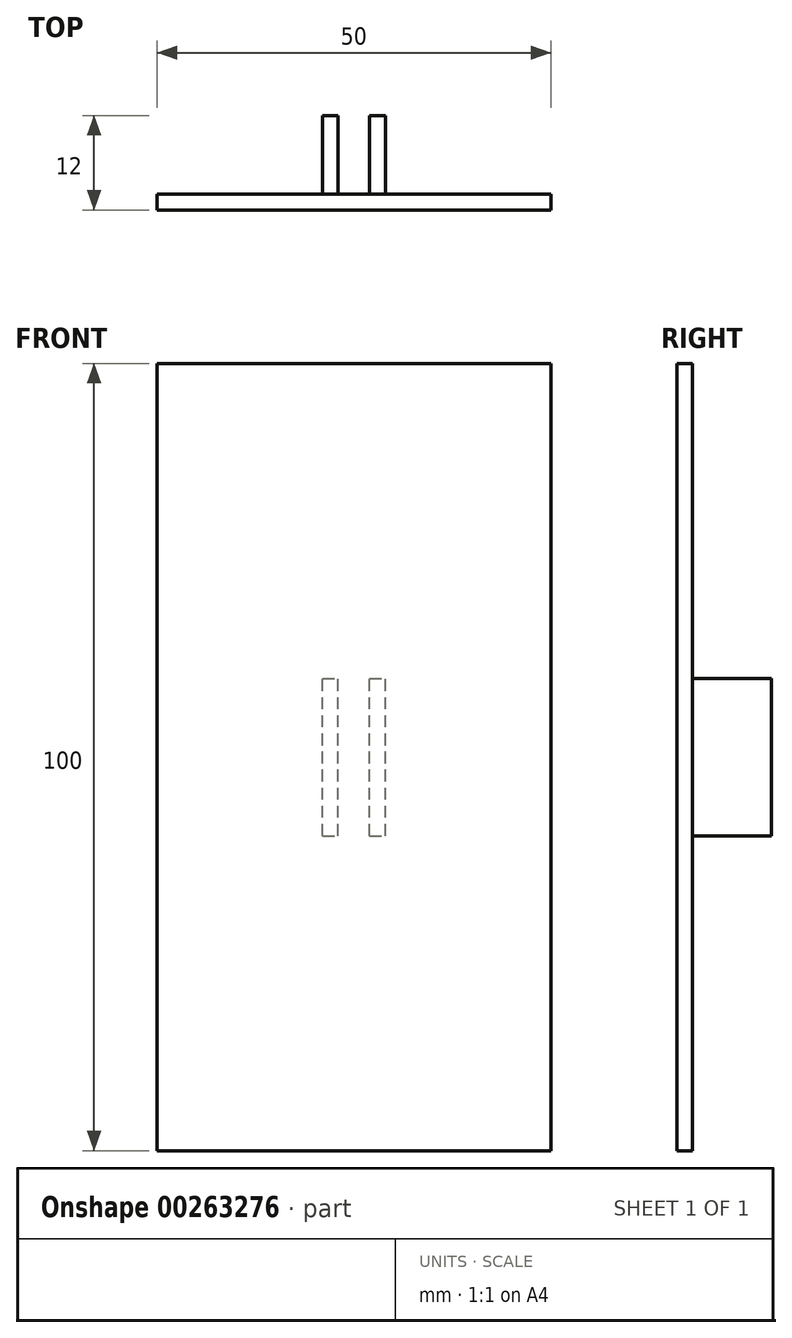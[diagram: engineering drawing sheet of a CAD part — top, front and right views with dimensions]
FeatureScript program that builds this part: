
annotation { "Feature Type Name" : "Feature", "Feature Type Description" : "" }
export const myFeature = defineFeature(function(context is Context, id is Id, definition is map)
    precondition{}
    {
        {
            var Q0;
            Q0=qCreatedBy(makeId("Front.planeOp"),FACE);
            var sketch = newSketch(context, id + "F0", { "sketchPlane" : qUnion([Q0])});
            skLineSegment(sketch, "E0.bottom", {"start": v(25, -50) * mm, "end": v(-25, -50) * mm});
            skLineSegment(sketch, "E0.top", {"start": v(25, 50) * mm, "end": v(-25, 50) * mm});
            skLineSegment(sketch, "E0.left", {"start": v(25, -50) * mm, "end": v(25, 50) * mm});
            skLineSegment(sketch, "E0.right", {"start": v(-25, -50) * mm, "end": v(-25, 50) * mm});
            skPoint(sketch, "E0.middle", {"position": v(0, 0) * mm});
            skSolve(sketch);
        }
        {
            var Q0;
            Q0=qSketchRegion(id+"F0",true);
            extrude(context, id + "F1", {"entities" : qUnion([Q0]), "depth" : 2 * mm});
        }
        {
            var Q0;
            Q0=makeQuery(id+"F1.opExtrude","CAP_FACE",FACE,{"disambiguationData":[OSD([sQuery(id+"F0.wireOp",EDGE,"E0.bottom"),sQuery(id+"F0.wireOp",EDGE,"E0.top"),sQuery(id+"F0.wireOp",EDGE,"E0.left"),sQuery(id+"F0.wireOp",EDGE,"E0.right")])],"isStart":true});
            var sketch = newSketch(context, id + "F2", { "sketchPlane" : qUnion([Q0])});
            skLineSegment(sketch, "E1.bottom", {"start": v(4, -10) * mm, "end": v(-4, -10) * mm});
            skLineSegment(sketch, "E1.top", {"start": v(4, 10) * mm, "end": v(-4, 10) * mm});
            skLineSegment(sketch, "E1.left", {"start": v(4, -10) * mm, "end": v(4, 10) * mm});
            skLineSegment(sketch, "E1.right", {"start": v(-4, -10) * mm, "end": v(-4, 10) * mm});
            skPoint(sketch, "E1.middle", {"position": v(0, 0) * mm});
            skSolve(sketch);
        }
        {
            var Q0;
            Q0 = qSketchRegion(id + "F2", true);
            extrude(context, id + "F3", {"entities" : qUnion([Q0]), "operationType" : NewBodyOperationType.ADD, "depth" : 10 * mm, "offsetDistance" : 25 * mm});
        }
        {
            var Q0;
            Q0=makeQuery(id+"F3.opExtrude","CAP_FACE",FACE,{"disambiguationData":[OSD([sQuery(id+"F2.wireOp",EDGE,"E1.bottom"),sQuery(id+"F2.wireOp",EDGE,"E1.top"),sQuery(id+"F2.wireOp",EDGE,"E1.left"),sQuery(id+"F2.wireOp",EDGE,"E1.right")])],"isStart":false});
            var sketch = newSketch(context, id + "F4", { "sketchPlane" : qUnion([Q0])});
            skLineSegment(sketch, "E2.bottom", {"start": v(2, -18.11) * mm, "end": v(-2, -18.11) * mm});
            skLineSegment(sketch, "E2.top", {"start": v(2, 18.11) * mm, "end": v(-2, 18.11) * mm});
            skLineSegment(sketch, "E2.left", {"start": v(2, -18.11) * mm, "end": v(2, 18.11) * mm});
            skLineSegment(sketch, "E2.right", {"start": v(-2, -18.11) * mm, "end": v(-2, 18.11) * mm});
            skPoint(sketch, "E2.middle", {"position": v(0, 0) * mm});
            skSolve(sketch);
        }
        {
            var Q0;
            Q0 = qSketchRegion(id + "F4", true);
            extrude(context, id + "F5", {"entities" : qUnion([Q0]), "operationType" : NewBodyOperationType.REMOVE, "oppositeDirection" : true, "depth" : 10 * mm, "offsetDistance" : 25 * mm});
        }
    });
